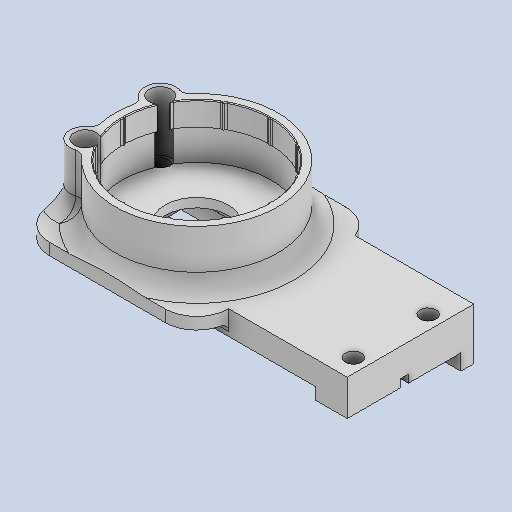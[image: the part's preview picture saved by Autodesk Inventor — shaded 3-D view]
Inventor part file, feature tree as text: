
AUTODESK INVENTOR PART (.ipt)
format: ipt  version: 2022 (Build 260153000, 153)  size: 642,560 bytes
history: native  units: mm
features: extrude x13, sketch x12, fillet x7, other x3, mirror x1, pattern_circular x1
ambient origin geometry x8: Origin, YZ Plane, XZ Plane, XY Plane, X Axis, Y Axis, Z Axis, Center Point
bodies: Body1 (feature_tree)
feature tree (37):
  extrude  "Выдавливание2"  Depth=28.6mm
  sketch  "Эскиз2"
  extrude  "Выдавливание3"  Depth=12.05mm
  extrude  "Выдавливание11"  Depth=31.58mm
  extrude  "Выдавливание12"  Depth=14.05mm
  extrude  "Выдавливание13"  Depth=29.1mm
  extrude  "Выдавливание14"  Depth=75.0mm
  other  "РабПлоскость2"
  mirror  "Зеркальное отражение2"
  extrude  "Выдавливание15"  Depth=3.0mm
  extrude  "Выдавливание18"  Depth=4.0mm TaperAngle=0.0deg
  fillet  "Сопряжение5"  Radius=4.1mm
  extrude  "Выдавливание19"  Depth=19.0mm
  fillet  "Сопряжение6"  Radius=68.0mm
  other  "РабОсь1"
  pattern_circular  "Круговой массив1"  [2 undecoded]
  extrude  "Выдавливание20"  Depth=4.1mm TaperAngle=0.0deg
  extrude  "Выдавливание21"  Depth=22.25mm
  fillet  "Сопряжение8"  Radius=16.0mm
  fillet  "Сопряжение9"  Radius=2.1mm
  other  "РабПлоскость4"
  extrude  "Выдавливание26"  Depth=59.05mm
  fillet  "Сопряжение10"  Radius=28.6mm
  extrude  "Выдавливание27"  Depth=4.475mm
  fillet  "Сопряжение11"  Radius=3.0mm
  fillet  "Сопряжение12"  Radius=4.0mm
  sketch  "Эскиз1"
  sketch  "Эскиз9"
  sketch  "Эскиз10"
  sketch  "Эскиз11"
  sketch  "Эскиз12"
  sketch  "Эскиз13"
  sketch  "Эскиз15"
  sketch  "Эскиз16"
  sketch  "Эскиз17"
  sketch  "Эскиз18"
  sketch  "Эскиз24"
note: 2 required parameter values undecoded (feature->parameter linkage not recoverable at this tier; creation-order binding heuristic only, values carry confidence <= 0.55)
